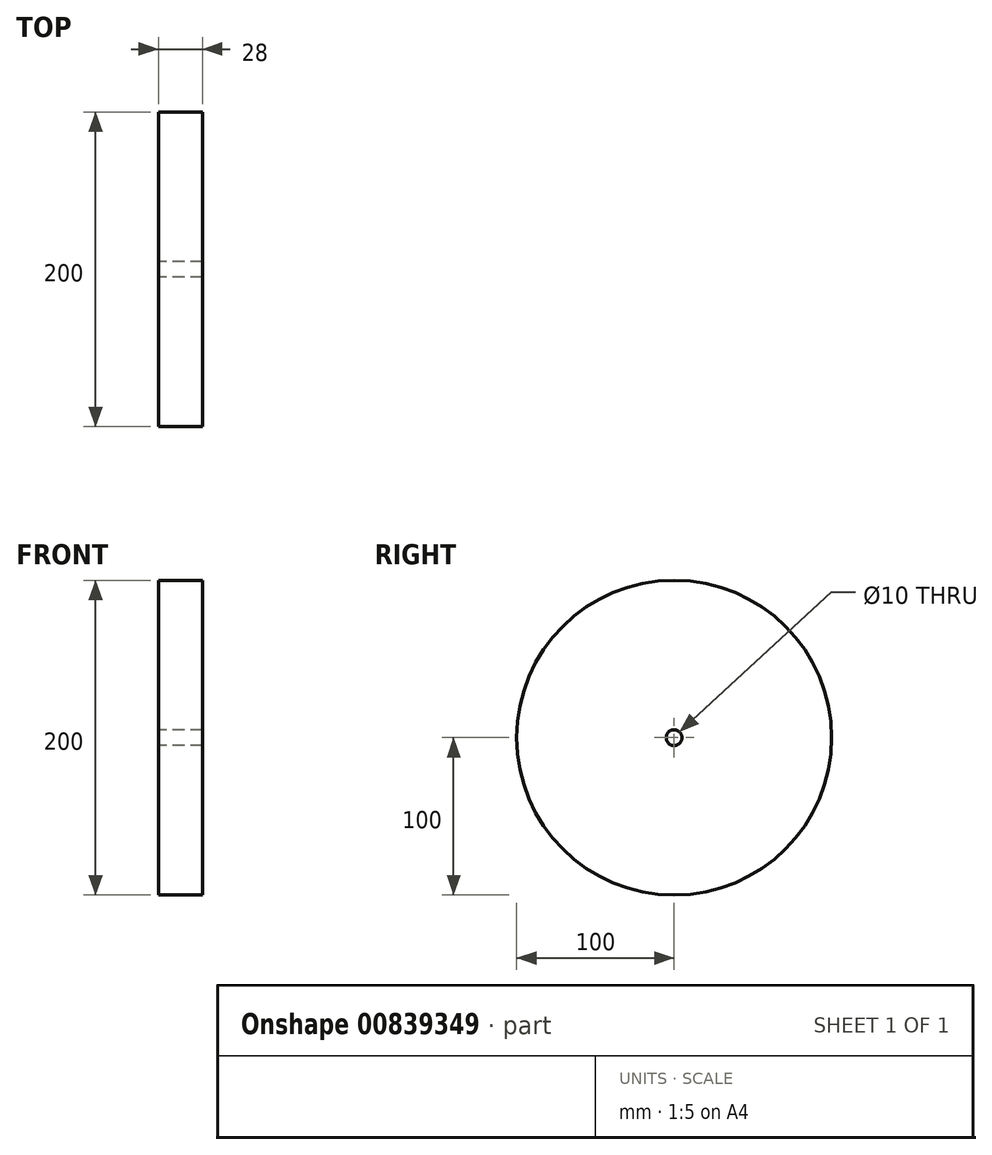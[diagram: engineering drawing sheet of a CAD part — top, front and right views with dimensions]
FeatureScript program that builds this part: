
annotation { "Feature Type Name" : "Feature", "Feature Type Description" : "" }
export const myFeature = defineFeature(function(context is Context, id is Id, definition is map)
    precondition{}
    {
        {
            var Q0;
            Q0=qCreatedBy(makeId("Right.planeOp"),FACE);
            var sketch = newSketch(context, id + "F0", { "sketchPlane" : qUnion([Q0])});
            skCircle(sketch, "E0", {"center": v(0, 0) * mm, "radius": 100 * mm});
            skCircle(sketch, "E1", {"center": v(0, 0) * mm, "radius": 5 * mm});
            skSolve(sketch);
        }
        {
            var Q0;
            Q0=qSketchRegion(id+"F0",true);
            extrude(context, id + "F1", {"entities" : qUnion([Q0]), "depth" : 28 * mm, "offsetDistance" : 25 * mm});
        }
    });
